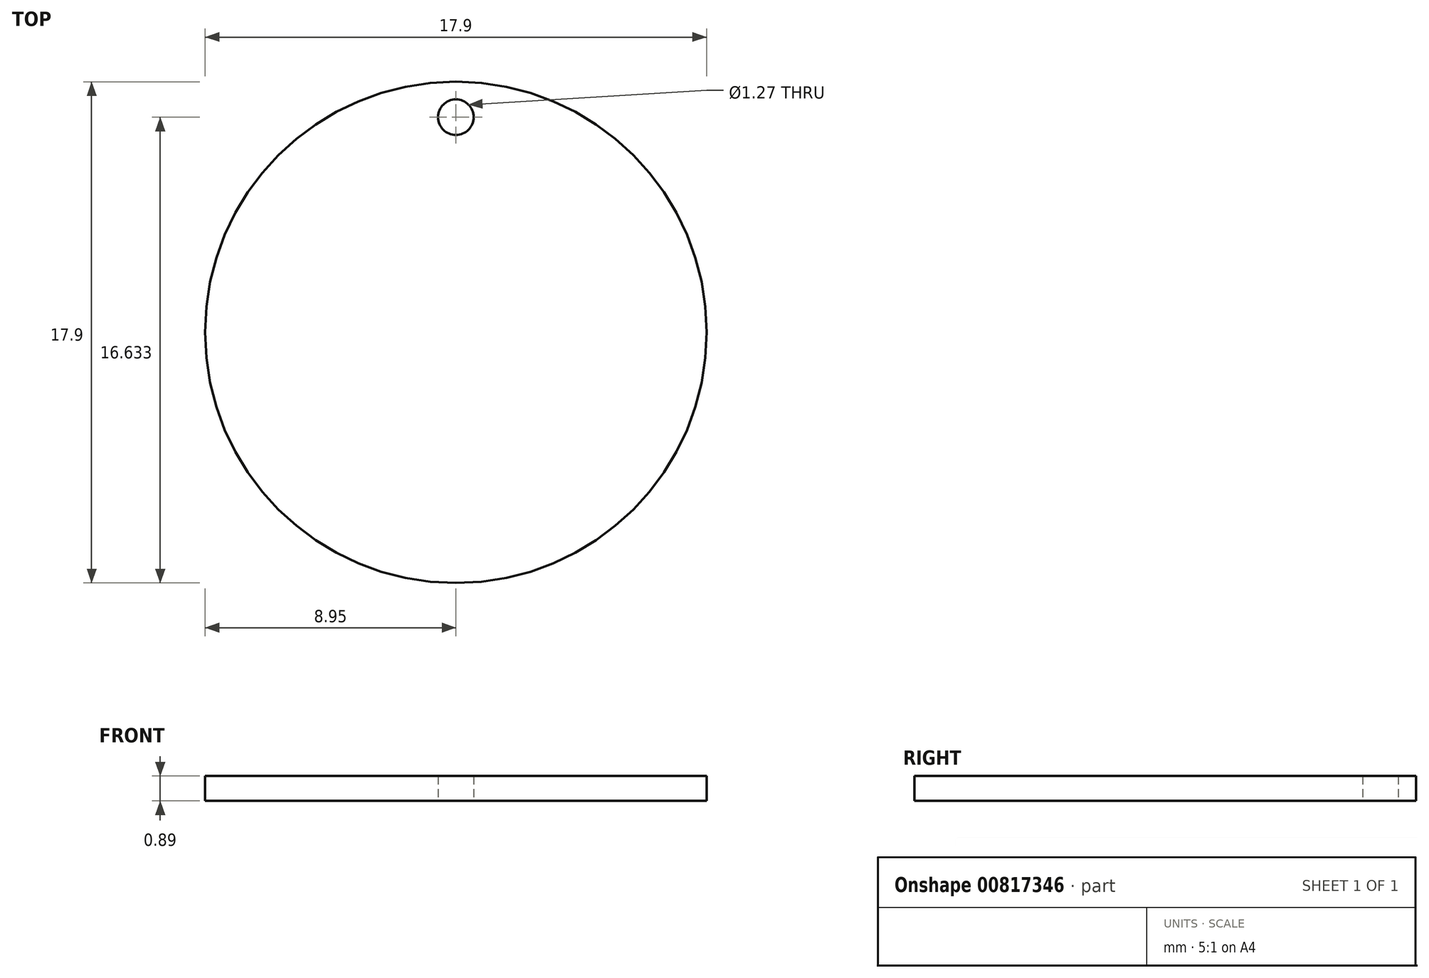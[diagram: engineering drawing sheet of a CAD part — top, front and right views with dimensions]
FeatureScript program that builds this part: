
annotation { "Feature Type Name" : "Feature", "Feature Type Description" : "" }
export const myFeature = defineFeature(function(context is Context, id is Id, definition is map)
    precondition{}
    {
        {
            var Q0;
            Q0=qCreatedBy(makeId("Top.planeOp"),FACE);
            var sketch = newSketch(context, id + "F0", { "sketchPlane" : qUnion([Q0])});
            skCircle(sketch, "E0", {"center": v(0, 0) * mm, "radius": 8.95 * mm});
            skCircle(sketch, "E1", {"center": v(0, 7.68) * mm, "radius": 0.64 * mm});
            skSolve(sketch);
        }
        {
            var Q0;
            Q0 = qSketchRegion(id + "F0", true);
            extrude(context, id + "F1", {"entities" : qUnion([Q0]), "depth" : 0.89 * mm, "offsetDistance" : 25.4 * mm});
        }
    });
